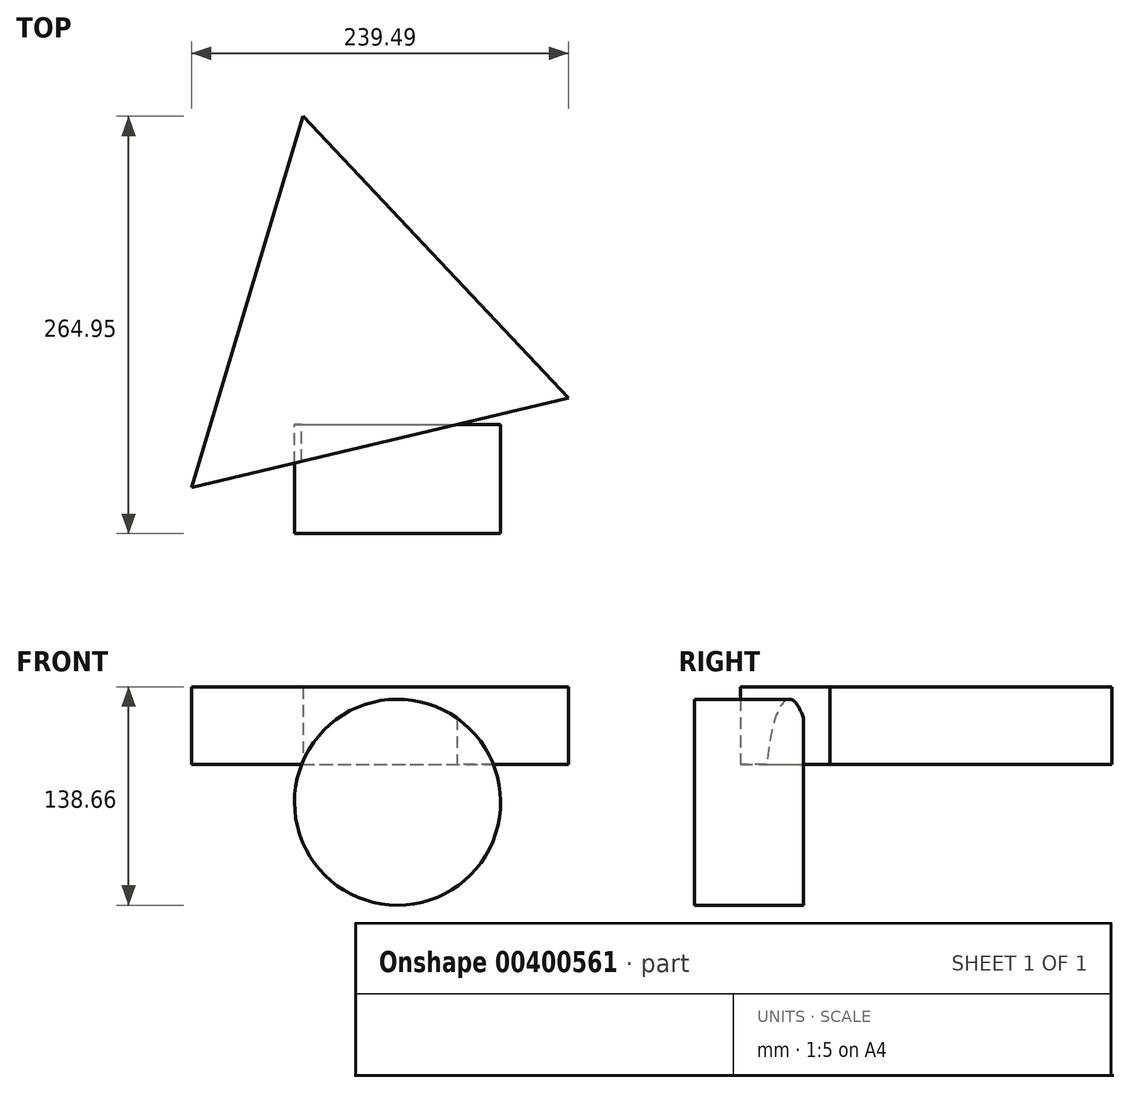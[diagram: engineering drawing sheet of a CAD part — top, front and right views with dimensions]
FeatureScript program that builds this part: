
annotation { "Feature Type Name" : "Feature", "Feature Type Description" : "" }
export const myFeature = defineFeature(function(context is Context, id is Id, definition is map)
    precondition{}
    {
        {
            var Q0;
            Q0=qCreatedBy(makeId("Top.planeOp"),FACE);
            var sketch = newSketch(context, id + "F0", { "sketchPlane" : qUnion([Q0])});
            skCircle(sketch, "E0.cCircle", {"center": v(-53.83, 57.6) * mm, "radius": 71.04 * mm, "construction": true});
            skLineSegment(sketch, "E0.0", {"start": v(82.26, 16.77) * mm, "end": v(-157.23, -39.85) * mm});
            skLineSegment(sketch, "E0.1", {"start": v(-157.23, -39.85) * mm, "end": v(-86.52, 195.86) * mm});
            skLineSegment(sketch, "E0.2", {"start": v(-86.52, 195.86) * mm, "end": v(82.26, 16.77) * mm});
            skPoint(sketch, "E0.0.midPoint", {"position": v(-37.49, -11.54) * mm});
            skSolve(sketch);
        }
        {
            var Q0;
            Q0 = qSketchRegion(id + "F0", true);
            extrude(context, id + "F1", {"entities" : qUnion([Q0]), "depth" : 49.28 * mm});
        }
        {
            var Q0;
            Q0=qCreatedBy(makeId("Front.planeOp"),FACE);
            var sketch = newSketch(context, id + "F2", { "sketchPlane" : qUnion([Q0])});
            skCircle(sketch, "E1", {"center": v(-26.47, -23.95) * mm, "radius": 65.42 * mm});
            skSolve(sketch);
        }
        {
            var Q0;
            Q0 = qSketchRegion(id + "F2", true);
            extrude(context, id + "F3", {"entities" : qUnion([Q0]), "operationType" : NewBodyOperationType.ADD, "depth" : 69.1 * mm});
        }
    });
